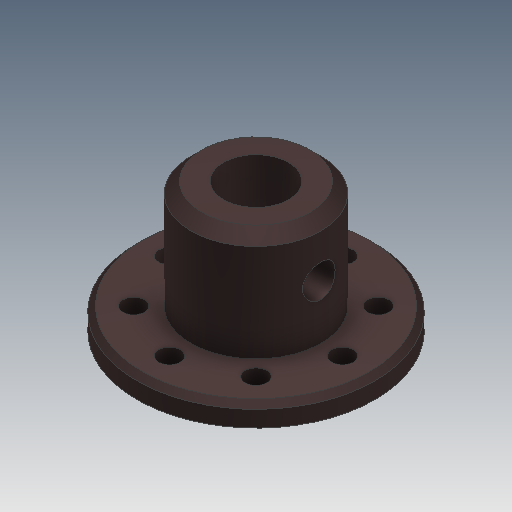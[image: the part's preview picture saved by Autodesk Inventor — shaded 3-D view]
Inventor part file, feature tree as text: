
AUTODESK INVENTOR PART (.ipt)
format: ipt  version: 2019 (Build 230136000, 136)  size: 175,104 bytes
history: native  units: mm
features: other x3, extrude x1, sketch x1
ambient origin geometry x8: Origin, YZ Plane, XZ Plane, XY Plane, X Axis, Y Axis, Z Axis, Center Point
bodies: Solid1 (feature_tree)
feature tree (5):
  other  "Servo-Dynamixel-Adapter.ipt"
  extrude  "Extrusion1"  Depth=3.0mm
  other  "Solid1::Servo-Dynamixel-Adapter.ipt"
  other  "TaggingFeature1"
  sketch  "Sketch1"  dims[d0=10.0mm d1=8.5mm d2=3.0mm d3=0.0mm]
